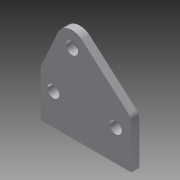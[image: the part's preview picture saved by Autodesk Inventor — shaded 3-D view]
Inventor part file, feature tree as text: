
AUTODESK INVENTOR PART (.ipt)
format: ipt  version: 2014 (Build 180170000, 170)  size: 103,936 bytes
history: native  units: in
note: dims shown in document units (in); Inventor stores cm internally (conversion verified against a paired STEP export)
features: extrude x1, fillet x1, sketch x1
ambient origin geometry x8: Origin, YZ Plane, XZ Plane, XY Plane, X Axis, Y Axis, Z Axis, Center Point
bodies: Solid1 (feature_tree)
feature tree (3):
  extrude  "Extrusion1"  Depth=0.125in TaperAngle=0.0deg
  fillet  "Fillet1"  Radius=0.5in
  sketch  "Sketch1"  dims[d1=0.19in d3=0.125in d4=0.0in d5=0.5in d6=0.25in d7=0.2in d9=0.25in d10=1.0in d14=0.5in d15=0.5in d16=0.194in d17=0.25in d18=0.125in]
